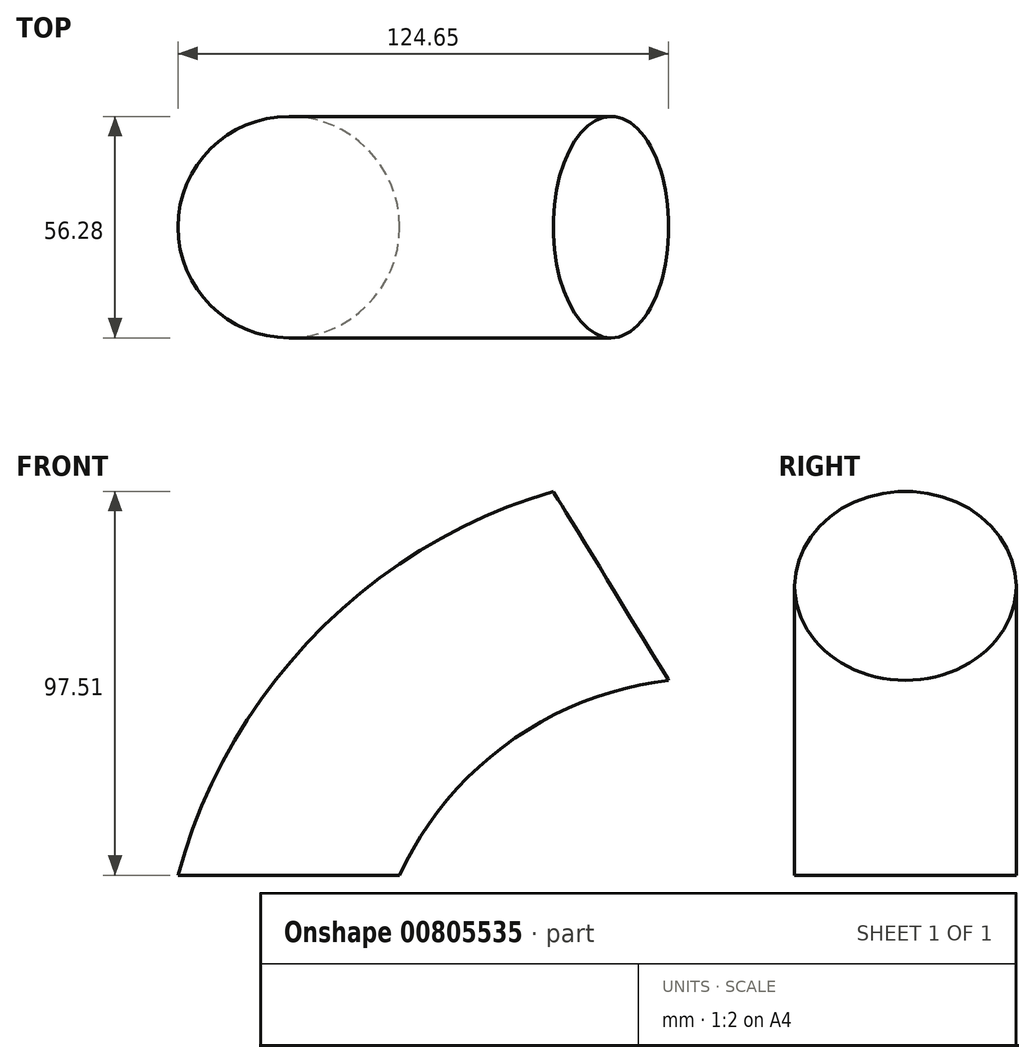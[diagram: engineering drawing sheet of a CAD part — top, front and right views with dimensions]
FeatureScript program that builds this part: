
annotation { "Feature Type Name" : "Feature", "Feature Type Description" : "" }
export const myFeature = defineFeature(function(context is Context, id is Id, definition is map)
    precondition{}
    {
        {
            var Q0;
            Q0=qCreatedBy(makeId("Top.planeOp"),FACE);
            var sketch = newSketch(context, id + "F0", { "sketchPlane" : qUnion([Q0])});
            skCircle(sketch, "E0", {"center": v(0, 0) * mm, "radius": 28.14 * mm});
            skSolve(sketch);
        }
        {
            var Q0;
            Q0=qCreatedBy(makeId("Front.planeOp"),FACE);
            var sketch = newSketch(context, id + "F1", { "sketchPlane" : qUnion([Q0])});
            skArc(sketch, "E1", {"start": v(81.85, 73.5) * mm, "mid": v(31.32, 47.44) * mm, "end": v(0, 0) * mm});
            skSolve(sketch);
        }
        {
            var Q0;
            Q0=makeQuery(id+"F0.imprint","IMPRINT",FACE,{"disambiguationData":[TD([[makeQuery(id+"F0.imprint","IMPRINT",EDGE,{"derivedFrom":sQuery(id+"F0.wireOp",EDGE,"E0")}),1.0]])]});
            var Q1;
            Q1=sQuery(id+"F1.wireOp",EDGE,"E1");
            sweep(context, id + "F2", {"profiles" : qUnion([Q0]), "path" : qUnion([Q1])});
        }
    });
